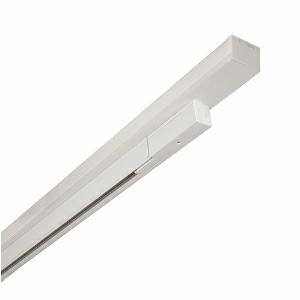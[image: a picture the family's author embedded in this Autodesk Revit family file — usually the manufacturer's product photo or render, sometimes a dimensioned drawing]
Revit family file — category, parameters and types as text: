
# Revit family: 3f_filippi_-_3f_linux_track_3f_filippi_-_a20424_-_3f_linux_tk_l1778
name_source: partatom
category: Furniture
units: mm (PartAtom-declared; Revit-internal decimal feet)

## family parameters
Cut with Voids When Loaded = No
Host = Face
Room Calculation Point = No
Shared = No

## types (1)
- 3F Filippi - 3F Linux Track
    Default Elevation = 1219 mm
    Description = Unit for structure continues 3F Linux S.

MECHANICAL
Light unit in hot-galvanised steel with white polyester powder coating, with retractable fastening clips and stainless steel safety hooks.
Electrified busbar made from extruded white aluminium, Eurostandard Plus compliant.
The wires are enclosed in rigid extruded profiles made of PVC insulating material with high dielectric strength.
Length of the electrified busbar: 1500 mm.
Dimensions: 1778x62 mm, height 90 mm. Weight 3.15 kg.
IP20 protection degree.
Glow-wire test resistance 960°C.

ELECTRICAL
CE - IEC 60598-1 - EN 60598-1.
Connection to the structure with mobile 7-pin plug with phase selection (H05Z-U Halogen Free cable section 0.5 mm² HT90).
(L1/L2/L3/N/GRD/DA/DA) 16A/440V 2x1A/50V FELV AC (DALI).
Copper conductors.

INSTALLATION
Ceiling / Suspended / Wall.
All accessories dedicated to this product are available on the Catalog and on our website www.3F-Filippi.com.

STRUCTURE
Hot-galvanised wired structure, painted in polyester base white, obtained through rolling process.
Saline-mist resistance equal to 300hrs and damp resistance equal to 700hrs.
Through-wiring 5 or 7 poles with cables H07Z-U Halogen Free section 2.5 mm² HT90, with quick connecting terminal, irreversible, start / end and intermediate power towers.
Linear connecting element in hot galvanised steel already mounted on one end to form continuous channels, only L3556 structures.
A20017 - 3F Linux S 5P L3556, structure with through-wiring 5-pole.
A20019 - 3F Linux S 5P L1778, structure with through-wiring 5-pole.
A20024 - 3F Linux S 7P L3556, structure with through-wiring 7-pole.
A20026 - 3F Linux S 7P L1778, structure with through-wiring 7-pole.

APPLICATIONS
In commercial environments, exhibition areas, shops and stores.

WARNING
Luminaire designed for disposal/recycling at end-of-life.
    Manufacturer = 3F Filippi
    Model = 3F Filippi - A20424 - 3F Linux TK L1778
    Product Name = 3F Filippi - 3F Linux Track
    RLX_Detail_Level = 0
    RlxData = <blob elided: 36121 chars, md5=14efec83>
    Type Comments = Product without accessories
    Type Image = 3ffilippi_3f_linux_track.jpg
    URL = http://relux.com

## geometry (parser evidence)
native form markers: Sweep x2
no freeform markers — native parametric forms only
